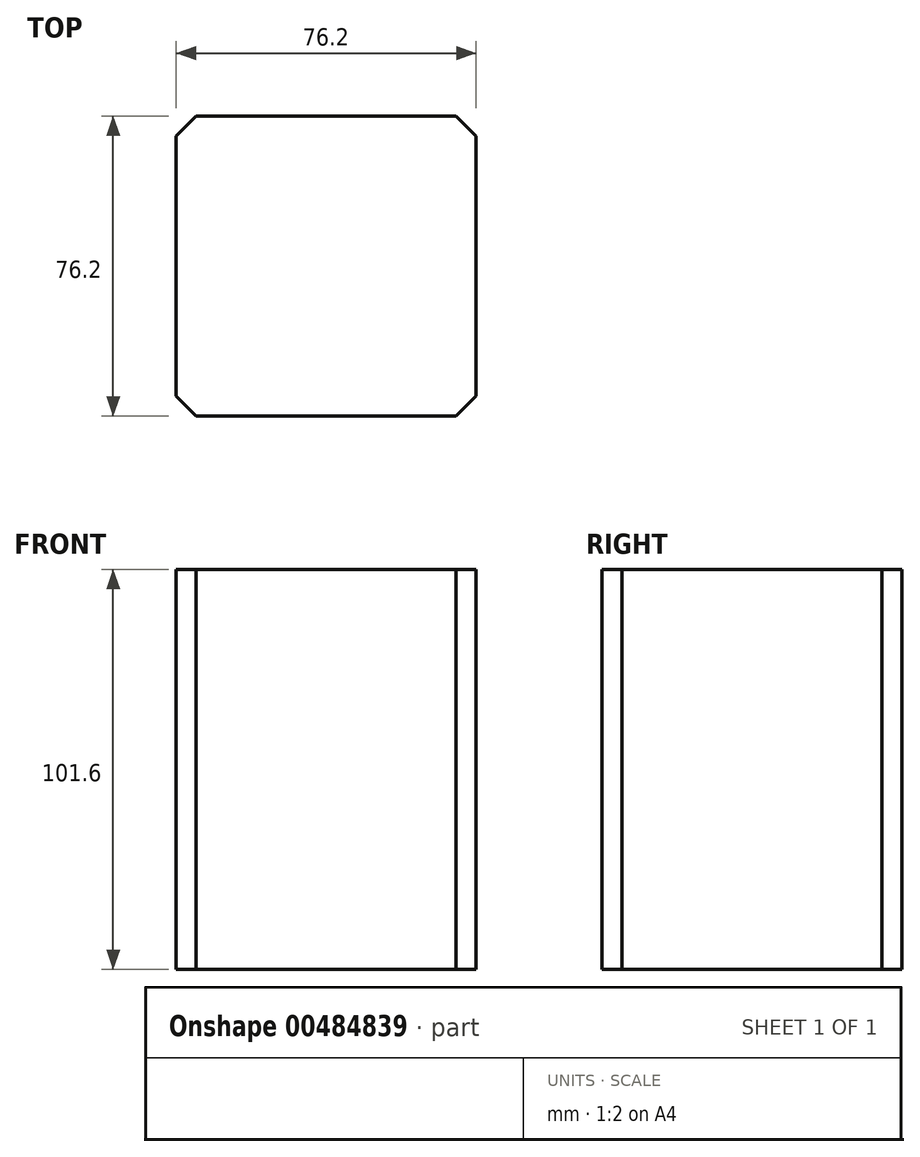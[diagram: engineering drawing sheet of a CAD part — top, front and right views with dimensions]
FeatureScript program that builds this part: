
annotation { "Feature Type Name" : "Feature", "Feature Type Description" : "" }
export const myFeature = defineFeature(function(context is Context, id is Id, definition is map)
    precondition{}
    {
        {
            var Q0;
            Q0=qCreatedBy(makeId("Top.planeOp"),FACE);
            var sketch = newSketch(context, id + "F0", { "sketchPlane" : qUnion([Q0])});
            skLineSegment(sketch, "E0.bottom", {"start": v(38.1, 38.1) * mm, "end": v(-38.1, 38.1) * mm});
            skLineSegment(sketch, "E0.top", {"start": v(38.1, -38.1) * mm, "end": v(-38.1, -38.1) * mm});
            skLineSegment(sketch, "E0.left", {"start": v(38.1, 38.1) * mm, "end": v(38.1, -38.1) * mm});
            skLineSegment(sketch, "E0.right", {"start": v(-38.1, 38.1) * mm, "end": v(-38.1, -38.1) * mm});
            skPoint(sketch, "E0.middle", {"position": v(0, 0) * mm});
            skSolve(sketch);
        }
        {
            var Q0;
            Q0 = qSketchRegion(id + "F0", true);
            extrude(context, id + "F1", {"entities" : qUnion([Q0]), "depth" : 101.6 * mm});
        }
        {
            var Q0;
            Q0=makeQuery(id+"F1.opExtrude","SWEPT_EDGE",EDGE,{"disambiguationData":[OSD([sQuery(id+"F0.wireOp",EDGE,"E0.top"),sQuery(id+"F0.wireOp",EDGE,"E0.right")])]});
            var Q1;
            Q1=makeQuery(id+"F1.opExtrude","SWEPT_EDGE",EDGE,{"disambiguationData":[OSD([sQuery(id+"F0.wireOp",EDGE,"E0.bottom"),sQuery(id+"F0.wireOp",EDGE,"E0.right")])]});
            var Q2;
            Q2=makeQuery(id+"F1.opExtrude","SWEPT_EDGE",EDGE,{"disambiguationData":[OSD([sQuery(id+"F0.wireOp",EDGE,"E0.top"),sQuery(id+"F0.wireOp",EDGE,"E0.left")])]});
            var Q3;
            Q3=makeQuery(id+"F1.opExtrude","SWEPT_EDGE",EDGE,{"disambiguationData":[OSD([sQuery(id+"F0.wireOp",EDGE,"E0.bottom"),sQuery(id+"F0.wireOp",EDGE,"E0.left")])]});
            chamfer(context, id + "F2", {"entities" : qUnion([Q0, Q1, Q2, Q3]), "width" : 5.08 * mm, "tangentPropagation" : true});
        }
    });
